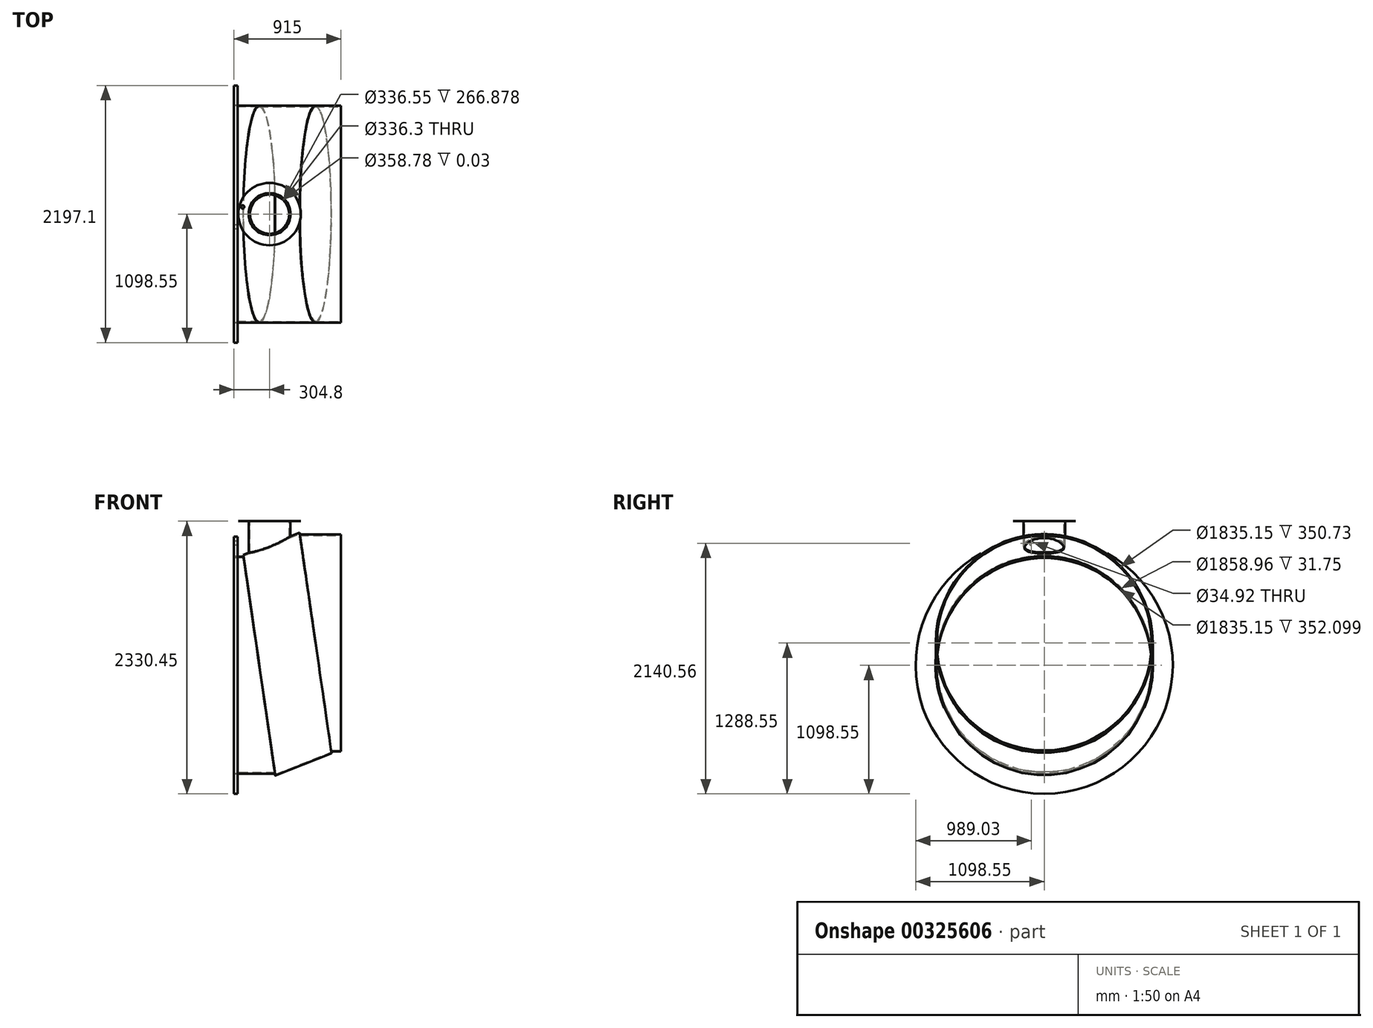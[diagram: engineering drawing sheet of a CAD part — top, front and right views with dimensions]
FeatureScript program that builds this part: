
annotation { "Feature Type Name" : "Feature", "Feature Type Description" : "" }
export const myFeature = defineFeature(function(context is Context, id is Id, definition is map)
    precondition{}
    {
        {
            var Q0;
            Q0=qCreatedBy(makeId("Front.planeOp"),FACE);
            var sketch = newSketch(context, id + "F0", { "sketchPlane" : qUnion([Q0])});
            skLineSegment(sketch, "E0", {"start": v(-240.4, -95) * mm, "end": v(240.4, 95) * mm, "construction": true});
            skLineSegment(sketch, "E1", {"start": v(240.4, 95) * mm, "end": v(457.5, 95) * mm, "construction": true});
            skLineSegment(sketch, "E2", {"start": v(-240.4, -95) * mm, "end": v(-457.5, -95) * mm, "construction": true});
            skLineSegment(sketch, "E3", {"start": v(-457.5, -95) * mm, "end": v(-457.5, 832.1) * mm, "construction": true});
            skLineSegment(sketch, "E4", {"start": v(-457.5, 832.1) * mm, "end": v(-374.95, 832.1) * mm, "construction": true});
            skLineSegment(sketch, "E5", {"start": v(-374.95, 832.1) * mm, "end": v(-240.4, -95) * mm, "construction": true});
            skLineSegment(sketch, "E6", {"start": v(457.5, 95) * mm, "end": v(457.5, -832.1) * mm, "construction": true});
            skLineSegment(sketch, "E7", {"start": v(457.5, -832.1) * mm, "end": v(374.95, -832.1) * mm, "construction": true});
            skLineSegment(sketch, "E8", {"start": v(374.95, -832.1) * mm, "end": v(240.4, 95) * mm, "construction": true});
            skLineSegment(sketch, "E9", {"start": v(-325.8, 824.45) * mm, "end": v(325.8, -824.45) * mm, "construction": true});
            skSolve(sketch);
        }
        {
            var Q0;
            Q0=sQuery(id+"F0.wireOp",VERTEX,"E2.end");
            var Q1;
            Q1=sQuery(id+"F0.wireOp",EDGE,"E2");
            cPlane(context, id + "F1", {"entities" : qUnion([Q0, Q1]), "cplaneType" : CPlaneType.LINE_POINT, "offset" : 25.4 * mm, "width" : 152.4 * mm, "height" : 152.4 * mm});
        }
        {
            var Q0;
            Q0=sQuery(id+"F0.wireOp",EDGE,"E0");
            cPlane(context, id + "F2", {"entities" : qUnion([Q0]), "cplaneType" : CPlaneType.MID_PLANE, "offset" : 25.4 * mm, "width" : 152.4 * mm, "height" : 152.4 * mm});
        }
        {
            var Q0;
            Q0=sQuery(id+"F0.wireOp",EDGE,"E1");
            var Q1;
            Q1=sQuery(id+"F0.wireOp",VERTEX,"E1.end");
            cPlane(context, id + "F3", {"entities" : qUnion([Q0, Q1]), "cplaneType" : CPlaneType.LINE_POINT, "offset" : 25.4 * mm, "width" : 152.4 * mm, "height" : 152.4 * mm});
        }
        {
            var Q0;
            Q0=qCreatedBy(id+"F1.planeOp",FACE);
            var sketch = newSketch(context, id + "F4", { "sketchPlane" : qUnion([Q0])});
            skPoint(sketch, "E10", {"position": v(0, -95) * mm});
            skCircle(sketch, "E11", {"center": v(0, -95) * mm, "radius": 927.1 * mm});
            skCircle(sketch, "E12", {"center": v(0, -95) * mm, "radius": 917.58 * mm});
            skSolve(sketch);
        }
        {
            var Q0;
            Q0=qCreatedBy(id+"F3.planeOp",FACE);
            var sketch = newSketch(context, id + "F5", { "sketchPlane" : qUnion([Q0])});
            skPoint(sketch, "E13", {"position": v(0, 95) * mm});
            skCircle(sketch, "E14", {"center": v(0, 95) * mm, "radius": 927.1 * mm});
            skCircle(sketch, "E15", {"center": v(0, 95) * mm, "radius": 917.58 * mm});
            skSolve(sketch);
        }
        {
            var Q0;
            Q0=qCreatedBy(id+"F2.planeOp",FACE);
            var sketch = newSketch(context, id + "F6", { "sketchPlane" : qUnion([Q0])});
            skPoint(sketch, "E16", {"position": v(0, 0) * mm});
            skCircle(sketch, "E17", {"center": v(0, 0) * mm, "radius": 927.1 * mm});
            skCircle(sketch, "E18", {"center": v(0, 0) * mm, "radius": 917.58 * mm});
            skSolve(sketch);
        }
        {
            var Q0;
            Q0=sQuery(id+"F0.wireOp",EDGE,"E5");
            cPlane(context, id + "F7", {"entities" : qUnion([Q0]), "cplaneType" : CPlaneType.LINE_ANGLE, "offset" : 25.4 * mm, "angle" : 0 * degree, "width" : 152.4 * mm, "height" : 152.4 * mm});
        }
        {
            var Q0;
            Q0=sQuery(id+"F0.wireOp",EDGE,"E8");
            cPlane(context, id + "F8", {"entities" : qUnion([Q0]), "cplaneType" : CPlaneType.LINE_ANGLE, "offset" : 25.4 * mm, "angle" : 0 * degree, "width" : 152.4 * mm, "height" : 152.4 * mm});
        }
        {
            var Q0;
            Q0=makeQuery(id+"F4.imprint","IMPRINT",FACE,{"disambiguationData":[TD([[makeQuery(id+"F4.imprint","IMPRINT",EDGE,{"derivedFrom":sQuery(id+"F4.wireOp",EDGE,"E11")}),1.0]])]});
            var Q1;
            Q1=qCreatedBy(id+"F7.planeOp",FACE);
            extrude(context, id + "F9", {"entities" : qUnion([Q0]), "endBound" : BoundingType.UP_TO_SURFACE, "oppositeDirection" : true, "depth" : 25.4 * mm, "endBoundEntityFace" : qUnion([Q1]), "offsetDistance" : 25.4 * mm});
        }
        {
            var Q0;
            Q0=makeQuery(id+"F6.imprint","IMPRINT",FACE,{"disambiguationData":[TD([[makeQuery(id+"F6.imprint","IMPRINT",EDGE,{"derivedFrom":sQuery(id+"F6.wireOp",EDGE,"E17")}),1.0]])]});
            var Q1;
            Q1=qCreatedBy(id+"F7.planeOp",FACE);
            extrude(context, id + "F10", {"entities" : qUnion([Q0]), "endBound" : BoundingType.UP_TO_SURFACE, "oppositeDirection" : true, "depth" : 25.4 * mm, "endBoundEntityFace" : qUnion([Q1]), "offsetDistance" : 25.4 * mm});
        }
        {
            var Q0;
            Q0=makeQuery(id+"F10.opExtrude","CAP_FACE",FACE,{"disambiguationData":[OSD([sQuery(id+"F6.wireOp",EDGE,"E17"),sQuery(id+"F6.wireOp",EDGE,"E18")])],"isStart":true});
            var Q1;
            Q1=qCreatedBy(id+"F8.planeOp",FACE);
            extrude(context, id + "F11", {"entities" : qUnion([Q0]), "operationType" : NewBodyOperationType.ADD, "endBound" : BoundingType.UP_TO_SURFACE, "depth" : 25.4 * mm, "endBoundEntityFace" : qUnion([Q1]), "offsetDistance" : 25.4 * mm});
        }
        {
            var Q0;
            Q0=makeQuery(id+"F5.imprint","IMPRINT",FACE,{"disambiguationData":[TD([[makeQuery(id+"F5.imprint","IMPRINT",EDGE,{"derivedFrom":sQuery(id+"F5.wireOp",EDGE,"E14")}),1.0]])]});
            var Q1;
            Q1=qCreatedBy(id+"F8.planeOp",FACE);
            extrude(context, id + "F12", {"entities" : qUnion([Q0]), "operationType" : NewBodyOperationType.ADD, "endBound" : BoundingType.UP_TO_SURFACE, "oppositeDirection" : true, "depth" : 25.4 * mm, "endBoundEntityFace" : qUnion([Q1]), "offsetDistance" : 25.4 * mm});
        }
        {
            var Q0;
            Q0=qCreatedBy(id+"F1.planeOp",FACE);
            var sketch = newSketch(context, id + "F13", { "sketchPlane" : qUnion([Q0])});
            skCircle(sketch, "E19", {"center": v(0, -95) * mm, "radius": 929.48 * mm});
            skCircle(sketch, "E20", {"center": v(0, -95) * mm, "radius": 1098.55 * mm});
            skCircle(sketch, "E21", {"center": v(0, -95) * mm, "radius": 1047.75 * mm, "construction": true});
            skLineSegment(sketch, "E22", {"start": v(0, -95) * mm, "end": v(0, 1104) * mm, "construction": true});
            skLineSegment(sketch, "E23", {"start": v(0, -95) * mm, "end": v(126.97, 1113.04) * mm, "construction": true});
            skPoint(sketch, "E24", {"position": v(109.52, 947.01) * mm});
            skSolve(sketch);
        }
        {
            var Q0;
            Q0=makeQuery(id+"F13.imprint","IMPRINT",FACE,{"disambiguationData":[TD([[makeQuery(id+"F13.imprint","IMPRINT",EDGE,{"derivedFrom":sQuery(id+"F13.wireOp",EDGE,"E19")}),-1.0]])]});
            extrude(context, id + "F14", {"entities" : qUnion([Q0]), "oppositeDirection" : true, "depth" : 31.75 * mm, "offsetDistance" : 25.4 * mm});
        }
        {
            var Q0;
            Q0=sQuery(id+"F13.wireOp",VERTEX,"E24");
            var Q1;
            Q1=makeQuery(id+"F14.opExtrude","SWEPT_BODY",BODY,{"disambiguationData":[OSD([sQuery(id+"F13.wireOp",EDGE,"E19"),sQuery(id+"F13.wireOp",EDGE,"E20")])]});
            hole(context, id + "F15", {"style" : HoleStyle.SIMPLE, "endStyle" : HoleEndStyle.BLIND, "holeDiameter" : 34.92 * mm, "majorDiameter" : 6.35 * mm, "holeDepth" : 31.75 * mm, "isTappedThrough" : true, "tappedDepth" : 12.7 * mm, "tapClearance" : 3, "startFromSketch" : true, "locations" : qUnion([Q0]), "scope" : qUnion([Q1])});
        }
        {
            var Q0;
            Q0=sQuery(id+"F0.wireOp",EDGE,"E2");
            cPlane(context, id + "F16", {"entities" : qUnion([Q0]), "cplaneType" : CPlaneType.LINE_ANGLE, "offset" : 25.4 * mm, "angle" : 90 * degree, "width" : 152.4 * mm, "height" : 152.4 * mm});
        }
        {
            var Q0;
            Q0=qCreatedBy(id+"F16.planeOp",FACE);
            cPlane(context, id + "F17", {"entities" : qUnion([Q0]), "cplaneType" : CPlaneType.OFFSET, "offset" : 927.1 * mm, "width" : 152.4 * mm, "height" : 152.4 * mm});
        }
        {
            var Q0;
            Q0=qCreatedBy(id+"F17.planeOp",FACE);
            cPlane(context, id + "F18", {"entities" : qUnion([Q0]), "cplaneType" : CPlaneType.OFFSET, "offset" : 304.8 * mm, "width" : 152.4 * mm, "height" : 152.4 * mm});
        }
        {
            var Q0;
            Q0=qCreatedBy(id+"F18.planeOp",FACE);
            var sketch = newSketch(context, id + "F19", { "sketchPlane" : qUnion([Q0])});
            skPoint(sketch, "E25.0", {"position": v(-457.5, 0) * mm});
            skCircle(sketch, "E26", {"center": v(-152.7, 0) * mm, "radius": 177.8 * mm});
            skCircle(sketch, "E27", {"center": v(-152.7, 0) * mm, "radius": 168.28 * mm});
            skCircle(sketch, "E28", {"center": v(-152.7, 0) * mm, "radius": 179.39 * mm});
            skCircle(sketch, "E29", {"center": v(-152.7, 0) * mm, "radius": 266.7 * mm});
            skCircle(sketch, "E30", {"center": v(-152.7, 0) * mm, "radius": 238.13 * mm, "construction": true});
            skLineSegment(sketch, "E31", {"start": v(-152.7, 0) * mm, "end": v(-510.67, 95.92) * mm, "construction": true});
            skPoint(sketch, "E32", {"position": v(-382.71, 61.63) * mm});
            skLineSegment(sketch, "E33", {"start": v(-152.7, 0) * mm, "end": v(-457.5, 0) * mm, "construction": true});
            skSolve(sketch);
        }
        {
            var Q0;
            Q0=makeQuery(id+"F19.imprint","IMPRINT",FACE,{"disambiguationData":[TD([[makeQuery(id+"F19.imprint","IMPRINT",EDGE,{"derivedFrom":sQuery(id+"F19.wireOp",EDGE,"E26")}),1.0]])]});
            extrude(context, id + "F20", {"entities" : qUnion([Q0]), "operationType" : NewBodyOperationType.ADD, "endBound" : BoundingType.UP_TO_NEXT, "oppositeDirection" : true, "depth" : 25.4 * mm, "offsetDistance" : 9.52 * mm, "offsetOppositeDirection" : true});
        }
        {
            var Q0;
            Q0=sQuery(id+"F19.wireOp",VERTEX,"E31.start");
            var Q1;
            Q1=makeQuery(id+"F10.opExtrude","SWEPT_BODY",BODY,{"disambiguationData":[OSD([sQuery(id+"F6.wireOp",EDGE,"E17"),sQuery(id+"F6.wireOp",EDGE,"E18")])]});
            hole(context, id + "F21", {"style" : HoleStyle.SIMPLE, "endStyle" : HoleEndStyle.BLIND, "holeDiameter" : 336.3 * mm, "majorDiameter" : 6.35 * mm, "holeDepth" : 304.8 * mm, "isTappedThrough" : true, "tappedDepth" : 12.7 * mm, "tapClearance" : 3, "startFromSketch" : true, "locations" : qUnion([Q0]), "scope" : qUnion([Q1])});
        }
        {
            var Q0;
            Q0=makeQuery(id+"F19.imprint","IMPRINT",FACE,{"disambiguationData":[TD([[makeQuery(id+"F19.imprint","IMPRINT",EDGE,{"derivedFrom":sQuery(id+"F19.wireOp",EDGE,"E28")}),-1.0]])]});
            extrude(context, id + "F22", {"entities" : qUnion([Q0]), "operationType" : NewBodyOperationType.ADD, "oppositeDirection" : true, "depth" : 3 / 101.6 * mm, "offsetDistance" : 25.4 * mm});
        }
        {
            var Q0;
            Q0=sQuery(id+"F19.wireOp",VERTEX,"E32");
            var Q1;
            Q1=makeQuery(id+"F22.opExtrude","SWEPT_BODY",BODY,{"disambiguationData":[OSD([sQuery(id+"F19.wireOp",EDGE,"E28"),sQuery(id+"F19.wireOp",EDGE,"E29")])]});
            hole(context, id + "F23", {"style" : HoleStyle.SIMPLE, "endStyle" : HoleEndStyle.BLIND, "standardTappedOrClearance" : lookupTablePath({ "fit" : "Normal (ASME)", "standard" : "ANSI", "size" : "1", "type" : "Clearance" }), "standardBlindInLast" : lookupTablePath({ "fit" : "Normal", "standard" : "ANSI", "engagement" : "75%", "pitch" : "8 tpi", "size" : "1", "type" : "Clearance & tapped" }), "holeDiameter" : 27.79 * mm, "majorDiameter" : 6.35 * mm, "holeDepth" : 38.1 * mm, "isTappedThrough" : true, "tappedDepth" : 12.7 * mm, "tapClearance" : 3, "startFromSketch" : true, "locations" : qUnion([Q0]), "scope" : qUnion([Q1])});
        }
    });
